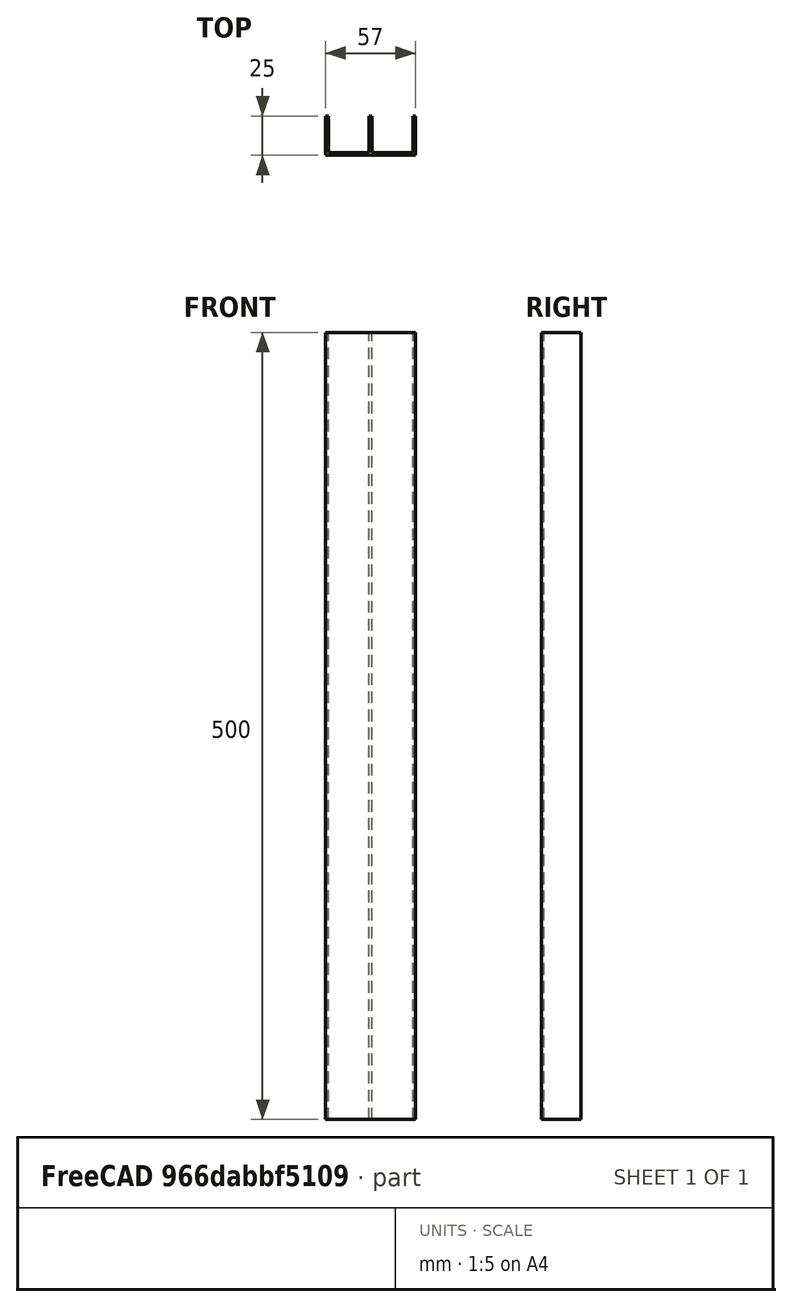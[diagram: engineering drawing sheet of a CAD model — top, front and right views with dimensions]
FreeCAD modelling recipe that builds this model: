
FCSTD DOCUMENT  (FreeCAD 0.20R29603 (Git))
Label: Trilho_RM013
License: All rights reserved
LicenseURL: http://en.wikipedia.org/wiki/All_rights_reserved
objects: Sketcher::SketchObject×1, PartDesign::Pad×1, PartDesign::Body×1, Spreadsheet::Sheet×1
note: 4 computed .brp shape members not serialized (recipe doc carries the construction recipe); baked Part::Feature solids carry a one-line shape summary decoded from their .brp

FEATURE [Sketcher::SketchObject] Sketch
  FullyConstrained = true
  MapMode = 5
  Support = -> [XY_Plane]
  expr: Constraints[24] = <<Params>>.width
  expr: Constraints[25] = <<Params>>.gap
  expr: Constraints[26] = <<Params>>.gap
  expr: Constraints[27] = <<Params>>.heigth
  expr: Constraints[30] = <<Params>>.thickness
  expr: Constraints[32] = <<Params>>.thickness
  sketch-geometry (12):
    g0: LineSegment StartX=-28.5 StartY=25 StartZ=0 EndX=-28.5 EndY=0 EndZ=0
    g1: LineSegment StartX=-28.5 StartY=0 StartZ=0 EndX=28.5 EndY=0 EndZ=0
    g2: LineSegment StartX=28.5 StartY=0 StartZ=0 EndX=28.5 EndY=25 EndZ=0
    g3: LineSegment StartX=28.5 StartY=25 StartZ=0 EndX=26.8333 EndY=25 EndZ=0
    g4: LineSegment StartX=26.8333 StartY=25 StartZ=0 EndX=26.8333 EndY=1.66667 EndZ=0
    g5: LineSegment StartX=26.8333 StartY=1.66667 StartZ=0 EndX=0.833333 EndY=1.66667 EndZ=0
    g6: LineSegment StartX=0.833333 StartY=1.66667 StartZ=0 EndX=0.833333 EndY=25 EndZ=0
    g7: LineSegment StartX=0.833333 StartY=25 StartZ=0 EndX=-0.833333 EndY=25 EndZ=0
    g8: LineSegment StartX=-0.833333 StartY=25 StartZ=0 EndX=-0.833333 EndY=1.66667 EndZ=0
    g9: LineSegment StartX=-0.833333 StartY=1.66667 StartZ=0 EndX=-26.8333 EndY=1.66667 EndZ=0
    g10: LineSegment StartX=-26.8333 StartY=1.66667 StartZ=0 EndX=-26.8333 EndY=25 EndZ=0
    g11: LineSegment StartX=-26.8333 StartY=25 StartZ=0 EndX=-28.5 EndY=25 EndZ=0
  constraints (35):
    c: PointOnObject(g0,g-1)
    c: Vertical(g0)
    c: Coincident(g1,g0)
    c: Vertical(g2)
    c: Horizontal(g3)
    c: Vertical(g4)
    c: Horizontal(g5)
    c: Vertical(g6)
    c: Vertical(g8)
    c: Horizontal(g9)
    c: Vertical(g10)
    c: Coincident(g11,g0)
    c: Coincident(g6,g7)
    c: Coincident(g4,g5)
    c: Coincident(g5,g6)
    c: Coincident(g4,g3)
    c: Coincident(g2,g3)
    c: Coincident(g1,g2)
    c: Coincident(g9,g10)
    c: Coincident(g9,g8)
    c: Coincident(g8,g7)
    c: Coincident(g11,g10)
    c: Horizontal(g11)
    c: Horizontal(g7)
    c: DistanceX(g0,g1) = 57
    c: DistanceX(g9,g8) = 26
    c: DistanceX(g5,g4) = 26
    c: DistanceY(g0,g0) = 25
    c: Horizontal(g0,g7)
    c: Horizontal(g7,g3)
    c: DistanceY(g1,g4) = 1.66667
    c: Horizontal(g8,g5)
    c: DistanceX(g0,g10) = 1.66667
    c: Equal(g11,g3)
    c: Symmetric(g0,g1,g-2)
FEATURE [PartDesign::Pad] Pad  label="Extrusion"
  Direction = (0,0,1)
  Length = 500
  Length2 = 10
  Profile = -> Sketch
  ReferenceAxis = -> Sketch [N_Axis]
  Type = 0
FEATURE [PartDesign::Body] Body
  Group = -> [Sketch,Pad]
  Origin = -> Origin
  Tip = -> Pad
FEATURE [Spreadsheet::Sheet] Spreadsheet  label="Params"
  cells = A1=length; B1(length)=500; A2=width; B2(width)=57; A3=heigth; B3(heigth)=25; A4=gap; B4(gap)=26; A5=thickness; B5(thickness)==(B2 - 2 * B4) / 3
